# Revit family: str
name_source: partatom
category: Generic Models
revit_build: Autodesk Revit 2014 (Build: 20130308_1515(x64)
units: mm (PartAtom-declared; Revit-internal decimal feet)

## types (6) — shared parameters
BODY = Bronze
Description = BRONZE STRAINERS -LL
Manufacturer = MIFAB
RETAINER CAP = Brass
URL = www.mifab.com

## per-type parameters (varying)
| type | 2h | 2w | 3AL | 3L | 3thk | A | B | C | C' | C'' | C3 | C4 | E | ID | Model | OUTR | RP1 | STR_SWT | cut |
| STR.50-SWT-BRZ-LL | 8 mm  [stored 0.0262467 ft] | 6 mm  [stored 0.019685 ft] | 1 mm  [stored 0.00328084 ft] | 4 mm  [stored 0.0131234 ft] | 0.8 mm  [stored 0.00262467 ft] | 70 mm | 35 mm  [stored 0.114829 ft] | 6 mm  [stored 0.019685 ft] | 55 mm | 4 mm  [stored 0.0131234 ft] | 3.25 mm | 57.5 mm | 10.23 mm | 5 mm  [stored 0.0164042 ft] | STR2.00-SWT-BRZ-LL | 6.5 mm | 6.5 mm | 13 mm | 4 mm  [stored 0.0131234 ft] |
| STR.75-SWT-BRZ-LL | 12 mm  [stored 0.0393701 ft] | 9 mm  [stored 0.0295276 ft] | 1.5 mm  [stored 0.00492126 ft] | 5 mm  [stored 0.0164042 ft] | 1 mm  [stored 0.00328084 ft] | 86 mm | 43 mm  [stored 0.141076 ft] | 6 mm  [stored 0.019685 ft] | 66 mm | 4.5 mm  [stored 0.0147638 ft] | 4 mm  [stored 0.0131234 ft] | 69 mm | 11.31 mm | 7 mm  [stored 0.0229659 ft] | STR0.75-SWT-BRZ-LL | 9.5 mm  [stored 0.031168 ft] | 9.5 mm  [stored 0.031168 ft] | 19 mm  [stored 0.062336 ft] | 5.5 mm  [stored 0.0180446 ft] |
| STR1.00-SWT-BRZ-LL | 15 mm  [stored 0.0492126 ft] | 10 mm  [stored 0.0328084 ft] | 2 mm  [stored 0.00656168 ft] | 7.5 mm  [stored 0.0246063 ft] | 2 mm  [stored 0.00656168 ft] | 95 mm | 54 mm | 13 mm | 82 mm | 8 mm  [stored 0.0262467 ft] | 8 mm  [stored 0.0262467 ft] | 87 mm | 11.31 mm | 10 mm  [stored 0.0328084 ft] | STR1.00-SWT-BRZ-LL | 12.5 mm  [stored 0.0410105 ft] | 12.5 mm  [stored 0.0410105 ft] | 25 mm  [stored 0.082021 ft] | 7 mm  [stored 0.0229659 ft] |
| STR1.25-SWT-BRZ-LL | 20 mm  [stored 0.0656168 ft] | 12 mm  [stored 0.0393701 ft] | 2.5 mm  [stored 0.0082021 ft] | 8 mm  [stored 0.0262467 ft] | 2 mm  [stored 0.00656168 ft] | 115 mm | 65 mm | 13 mm | 98 mm | 9 mm  [stored 0.0295276 ft] | 8 mm  [stored 0.0262467 ft] | 103 mm | 11.31 mm | 12 mm  [stored 0.0393701 ft] | STR1.25-SWT-BRZ-LL | 16 mm  [stored 0.0524934 ft] | 16 mm  [stored 0.0524934 ft] | 32 mm  [stored 0.104987 ft] | 10 mm  [stored 0.0328084 ft] |
| STR1.50-SWT-BRZ-LL | 25 mm  [stored 0.082021 ft] | 10 mm  [stored 0.0328084 ft] | 3.5 mm  [stored 0.0114829 ft] | 9 mm  [stored 0.0295276 ft] | 2 mm  [stored 0.00656168 ft] | 135 mm | 76 mm | 19 mm  [stored 0.062336 ft] | 113 mm | 12 mm  [stored 0.0393701 ft] | 12 mm  [stored 0.0393701 ft] | 120 mm | 11.31 mm | 16 mm  [stored 0.0524934 ft] | STR1.50-SWT-BRZ-LL | 20 mm  [stored 0.0656168 ft] | 20 mm  [stored 0.0656168 ft] | 40 mm  [stored 0.131234 ft] | 11 mm  [stored 0.0360892 ft] |
| STR2.00-SWT-BRZ-LL | 30 mm  [stored 0.0984252 ft] | 13.5 mm  [stored 0.0442913 ft] | 4 mm  [stored 0.0131234 ft] | 11.23 mm | 2 mm  [stored 0.00656168 ft] | 157.16 mm | 88.9 mm | 25 mm  [stored 0.082021 ft] | 130 mm | 15 mm  [stored 0.0492126 ft] | 15 mm  [stored 0.0492126 ft] | 138 mm | 11.31 mm | 21 mm  [stored 0.0688976 ft] | STR2.00-SWT-BRZ-LL | 25.5 mm  [stored 0.0836614 ft] | 25.5 mm  [stored 0.0836614 ft] | 51 mm | 13.53 mm |

note: [stored X ft] marks values corroborated as IEEE doubles in the binary element streams (Revit-internal decimal feet)

## geometry (parser evidence)
native form markers: Sweep x1
no freeform markers — native parametric forms only
